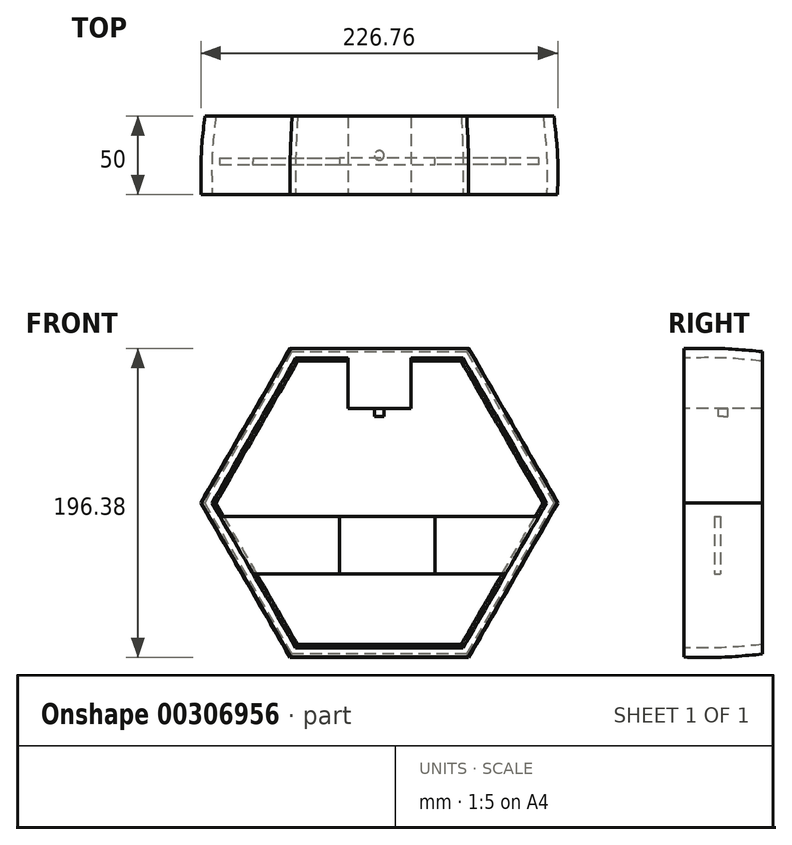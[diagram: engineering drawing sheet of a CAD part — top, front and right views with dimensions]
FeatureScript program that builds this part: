
annotation { "Feature Type Name" : "Feature", "Feature Type Description" : "" }
export const myFeature = defineFeature(function(context is Context, id is Id, definition is map)
    precondition{}
    {
        {
            var Q0;
            Q0=qCreatedBy(makeId("Front.planeOp"),FACE);
            var sketch = newSketch(context, id + "F0", { "sketchPlane" : qUnion([Q0])});
            skCircle(sketch, "E0.cCircle", {"center": v(0, 0) * mm, "radius": 98 * mm, "construction": true});
            skLineSegment(sketch, "E0.0", {"start": v(-56.58, 98) * mm, "end": v(56.58, 98) * mm});
            skLineSegment(sketch, "E0.1", {"start": v(56.58, 98) * mm, "end": v(113.16, 0) * mm});
            skLineSegment(sketch, "E0.2", {"start": v(113.16, 0) * mm, "end": v(56.58, -98) * mm});
            skLineSegment(sketch, "E0.3", {"start": v(56.58, -98) * mm, "end": v(-56.58, -98) * mm});
            skLineSegment(sketch, "E0.4", {"start": v(-56.58, -98) * mm, "end": v(-113.16, 0) * mm});
            skLineSegment(sketch, "E0.5", {"start": v(-113.16, 0) * mm, "end": v(-56.58, 98) * mm});
            skPoint(sketch, "E0.0.midPoint", {"position": v(0, 98) * mm});
            skSolve(sketch);
        }
        {
            var Q0;
            Q0=qCreatedBy(makeId("Front.planeOp"),FACE);
            cPlane(context, id + "F1", {"entities" : qUnion([Q0]), "cplaneType" : CPlaneType.OFFSET, "offset" : 25 * mm, "oppositeDirection" : true, "width" : 150 * mm, "height" : 150 * mm});
        }
        {
            var Q0;
            Q0=qCreatedBy(id+"F1.planeOp",FACE);
            var sketch = newSketch(context, id + "F2", { "sketchPlane" : qUnion([Q0])});
            skCircle(sketch, "E1.cCircle", {"center": v(0, 0) * mm, "radius": 96 * mm, "construction": true});
            skLineSegment(sketch, "E1.0", {"start": v(-55.43, 96) * mm, "end": v(55.43, 96) * mm});
            skLineSegment(sketch, "E1.1", {"start": v(55.43, 96) * mm, "end": v(110.85, 0) * mm});
            skLineSegment(sketch, "E1.2", {"start": v(110.85, 0) * mm, "end": v(55.43, -96) * mm});
            skLineSegment(sketch, "E1.3", {"start": v(55.43, -96) * mm, "end": v(-55.43, -96) * mm});
            skLineSegment(sketch, "E1.4", {"start": v(-55.43, -96) * mm, "end": v(-110.85, 0) * mm});
            skLineSegment(sketch, "E1.5", {"start": v(-110.85, 0) * mm, "end": v(-55.43, 96) * mm});
            skPoint(sketch, "E1.0.midPoint", {"position": v(0, 96) * mm});
            skSolve(sketch);
        }
        {
            var Q0;
            Q0=qCreatedBy(makeId("Front.planeOp"),FACE);
            cPlane(context, id + "F3", {"entities" : qUnion([Q0]), "cplaneType" : CPlaneType.OFFSET, "offset" : 25 * mm, "width" : 150 * mm, "height" : 150 * mm});
        }
        {
            var Q0;
            Q0=qCreatedBy(id+"F3.planeOp",FACE);
            var sketch = newSketch(context, id + "F4", { "sketchPlane" : qUnion([Q0])});
            skCircle(sketch, "E2.cCircle", {"center": v(0, 0) * mm, "radius": 98 * mm, "construction": true});
            skLineSegment(sketch, "E2.0", {"start": v(56.58, -98) * mm, "end": v(-56.58, -98) * mm});
            skLineSegment(sketch, "E2.1", {"start": v(-56.58, -98) * mm, "end": v(-113.16, 0) * mm});
            skLineSegment(sketch, "E2.2", {"start": v(-113.16, 0) * mm, "end": v(-56.58, 98) * mm});
            skLineSegment(sketch, "E2.3", {"start": v(-56.58, 98) * mm, "end": v(56.58, 98) * mm});
            skLineSegment(sketch, "E2.4", {"start": v(56.58, 98) * mm, "end": v(113.16, 0) * mm});
            skLineSegment(sketch, "E2.5", {"start": v(113.16, 0) * mm, "end": v(56.58, -98) * mm});
            skPoint(sketch, "E2.0.midPoint", {"position": v(0, -98) * mm});
            skSolve(sketch);
        }
        {
            var Q0;
            Q0=makeQuery(id+"F2.imprint","IMPRINT",FACE,{"disambiguationData":[TD([[makeQuery(id+"F2.imprint","IMPRINT",EDGE,{"derivedFrom":sQuery(id+"F2.wireOp",EDGE,"E1.0")}),-1.0]])]});
            var Q1;
            Q1=makeQuery(id+"F0.imprint","IMPRINT",FACE,{"disambiguationData":[TD([[makeQuery(id+"F0.imprint","IMPRINT",EDGE,{"derivedFrom":sQuery(id+"F0.wireOp",EDGE,"E0.0")}),-1.0]])]});
            var Q2;
            Q2=makeQuery(id+"F4.imprint","IMPRINT",FACE,{"disambiguationData":[TD([[makeQuery(id+"F4.imprint","IMPRINT",EDGE,{"derivedFrom":sQuery(id+"F4.wireOp",EDGE,"E2.0")}),-1.0]])]});
            loft(context, id + "F5", {"sheetProfilesArray" : [{ "sheetProfileEntities" : qUnion([Q0]) }, { "sheetProfileEntities" : qUnion([Q1]) }, { "sheetProfileEntities" : qUnion([Q2]) }]});
        }
        {
            var Q0;
            Q0=makeQuery(id+"F5.opLoft","CAP_FACE",FACE,{"disambiguationData":[OSD([makeQuery(id+"F2.imprint","IMPRINT",FACE,{"disambiguationData":[TD([[makeQuery(id+"F2.imprint","IMPRINT",EDGE,{"derivedFrom":sQuery(id+"F2.wireOp",EDGE,"E1.0")}),-1.0]])]})])],"isStart":true});
            var Q1;
            Q1=makeQuery(id+"F5.opLoft","CAP_FACE",FACE,{"disambiguationData":[OSD([makeQuery(id+"F4.imprint","IMPRINT",FACE,{"disambiguationData":[TD([[makeQuery(id+"F4.imprint","IMPRINT",EDGE,{"derivedFrom":sQuery(id+"F4.wireOp",EDGE,"E2.0")}),-1.0]])]})])],"isStart":true});
            shell(context, id + "F6", {"entities" : qUnion([Q0, Q1]), "thickness" : 6 * mm});
        }
        {
            var Q0;
            Q0=qCreatedBy(makeId("Top.planeOp"),FACE);
            cPlane(context, id + "F7", {"entities" : qUnion([Q0]), "cplaneType" : CPlaneType.OFFSET, "offset" : 45 * mm, "oppositeDirection" : true, "width" : 150 * mm, "height" : 150 * mm});
        }
        {
            var Q0;
            Q0=qCreatedBy(id+"F7.planeOp",FACE);
            var sketch = newSketch(context, id + "F8", { "sketchPlane" : qUnion([Q0])});
            skLineSegment(sketch, "E3", {"start": v(35.37, -1.71) * mm, "end": v(-25.32, -1.71) * mm});
            skLineSegment(sketch, "E4", {"start": v(-25.32, -1.71) * mm, "end": v(-25.32, -5.71) * mm});
            skLineSegment(sketch, "E5", {"start": v(-25.32, -5.71) * mm, "end": v(35.37, -5.71) * mm});
            skLineSegment(sketch, "E6", {"start": v(35.37, -5.71) * mm, "end": v(35.37, -1.71) * mm});
            skSolve(sketch);
        }
        {
            var Q0;
            Q0 = qSketchRegion(id + "F8", true);
            extrude(context, id + "F9", {"entities" : qUnion([Q0]), "depth" : 36.5 * mm});
        }
        {
            var Q0;
            Q0=makeQuery(id+"F9.opExtrude","SWEPT_FACE",FACE,{"disambiguationData":[OSD([sQuery(id+"F8.wireOp",EDGE,"E4")])]});
            extrude(context, id + "F10", {"entities" : qUnion([Q0]), "endBound" : BoundingType.UP_TO_NEXT, "depth" : 25 * mm});
        }
        {
            var Q0;
            Q0=makeQuery(id+"F9.opExtrude","SWEPT_FACE",FACE,{"disambiguationData":[OSD([sQuery(id+"F8.wireOp",EDGE,"E6")])]});
            extrude(context, id + "F11", {"entities" : qUnion([Q0]), "endBound" : BoundingType.UP_TO_NEXT, "depth" : 25 * mm});
        }
        {
            var Q0;
            Q0=qCreatedBy(makeId("Top.planeOp"),FACE);
            cPlane(context, id + "F12", {"entities" : qUnion([Q0]), "cplaneType" : CPlaneType.OFFSET, "offset" : 60 * mm, "width" : 150 * mm, "height" : 150 * mm});
        }
        {
            var Q0;
            Q0=qCreatedBy(id+"F12.planeOp",FACE);
            var sketch = newSketch(context, id + "F13", { "sketchPlane" : qUnion([Q0])});
            skLineSegment(sketch, "E7.0", {"start": v(-20, 25) * mm, "end": v(20, 25) * mm});
            skLineSegment(sketch, "E7.1", {"start": v(-20, -25) * mm, "end": v(20, -25) * mm});
            skLineSegment(sketch, "E8.left", {"start": v(-20, 25) * mm, "end": v(-20, -25) * mm});
            skLineSegment(sketch, "E8.right", {"start": v(20, 25) * mm, "end": v(20, -25) * mm});
            skPoint(sketch, "E8.middle", {"position": v(0, 0) * mm});
            skPoint(sketch, "E9.orphan", {"position": v(55.43, 25) * mm});
            skPoint(sketch, "E10.orphan", {"position": v(56.58, -25) * mm});
            skPoint(sketch, "E11.orphan", {"position": v(-56.58, -25) * mm});
            skPoint(sketch, "E12.orphan", {"position": v(-55.43, 25) * mm});
            skSolve(sketch);
        }
        {
            var Q0;
            Q0 = qSketchRegion(id + "F13", true);
            extrude(context, id + "F14", {"entities" : qUnion([Q0]), "operationType" : NewBodyOperationType.ADD, "endBound" : BoundingType.UP_TO_NEXT, "depth" : 25 * mm});
        }
        {
            var Q0;
            Q0=makeQuery(id+"F14.opExtrude","CAP_FACE",FACE,{"disambiguationData":[OSD([sQuery(id+"F13.wireOp",EDGE,"E7.0"),sQuery(id+"F13.wireOp",EDGE,"E7.1"),sQuery(id+"F13.wireOp",EDGE,"E8.left"),sQuery(id+"F13.wireOp",EDGE,"E8.right")])],"isStart":true});
            var sketch = newSketch(context, id + "F15", { "sketchPlane" : qUnion([Q0])});
            skCircle(sketch, "E13", {"center": v(0, 0) * mm, "radius": 3 * mm});
            skSolve(sketch);
        }
        {
            var Q0;
            Q0 = qSketchRegion(id + "F15", true);
            extrude(context, id + "F16", {"entities" : qUnion([Q0]), "operationType" : NewBodyOperationType.ADD, "depth" : 5 * mm});
        }
    });
